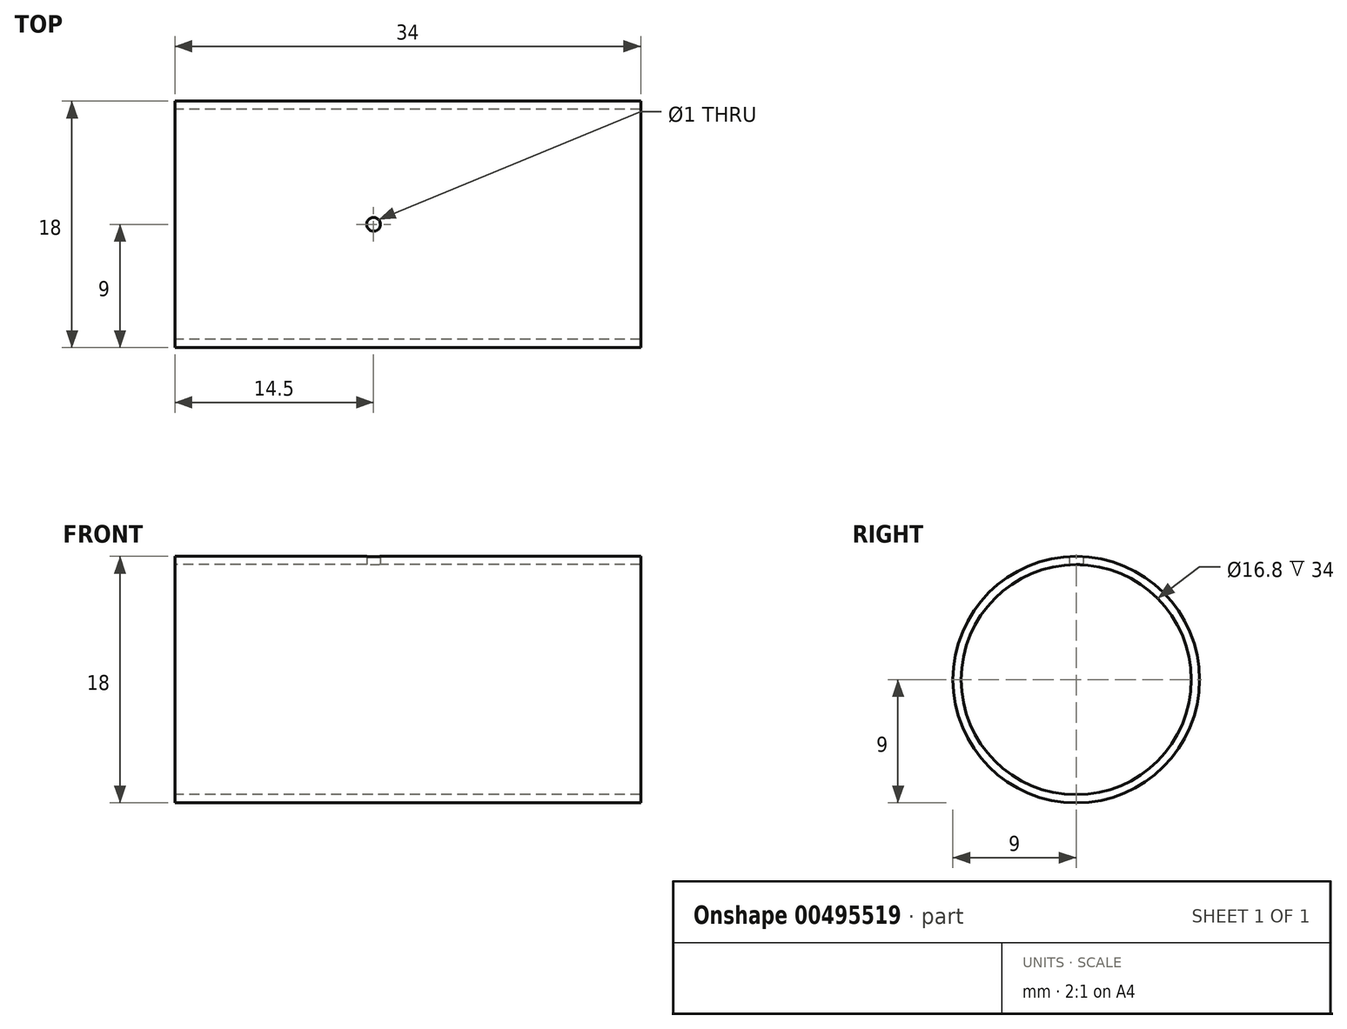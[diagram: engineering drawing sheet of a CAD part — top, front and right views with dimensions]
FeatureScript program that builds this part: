
annotation { "Feature Type Name" : "Feature", "Feature Type Description" : "" }
export const myFeature = defineFeature(function(context is Context, id is Id, definition is map)
    precondition{}
    {
        {
            var Q0;
            Q0=qCreatedBy(makeId("Right.planeOp"),FACE);
            var sketch = newSketch(context, id + "F0", { "sketchPlane" : qUnion([Q0])});
            skCircle(sketch, "E0", {"center": v(0, 0) * mm, "radius": 9 * mm});
            skCircle(sketch, "E1", {"center": v(0, 0) * mm, "radius": 8.4 * mm});
            skSolve(sketch);
        }
        {
            var Q0;
            Q0=qSketchRegion(id+"F0",true);
            extrude(context, id + "F1", {"entities" : qUnion([Q0]), "depth" : 34 * mm});
        }
        {
            var Q0;
            Q0=qCreatedBy(makeId("Front.planeOp"),FACE);
            var sketch = newSketch(context, id + "F2", { "sketchPlane" : qUnion([Q0])});
            skLineSegment(sketch, "E2.top", {"start": v(14.5, 6) * mm, "end": v(14, 6) * mm});
            skLineSegment(sketch, "E2.right", {"start": v(14, 9) * mm, "end": v(14, 6) * mm});
            skPoint(sketch, "E2.middle", {"position": v(14.5, 9) * mm});
            skLineSegment(sketch, "E3", {"start": v(14.5, 9) * mm, "end": v(14.5, 6) * mm});
            skPoint(sketch, "E3.endSnap0", {"position": v(14.5, 6) * mm});
            skLineSegment(sketch, "E4", {"start": v(14.5, 9) * mm, "end": v(14, 9) * mm});
            skSolve(sketch);
        }
        {
            var Q0;
            Q0=qSketchRegion(id+"F2",true);
            var Q1;
            Q1=sQuery(id+"F2.wireOp",EDGE,"E3");
            revolve(context, id + "F3", {"operationType" : NewBodyOperationType.REMOVE, "entities" : qUnion([Q0]), "axis" : qUnion([Q1]), "revolveType" : RevolveType.FULL, "oppositeDirection" : true});
        }
    });
